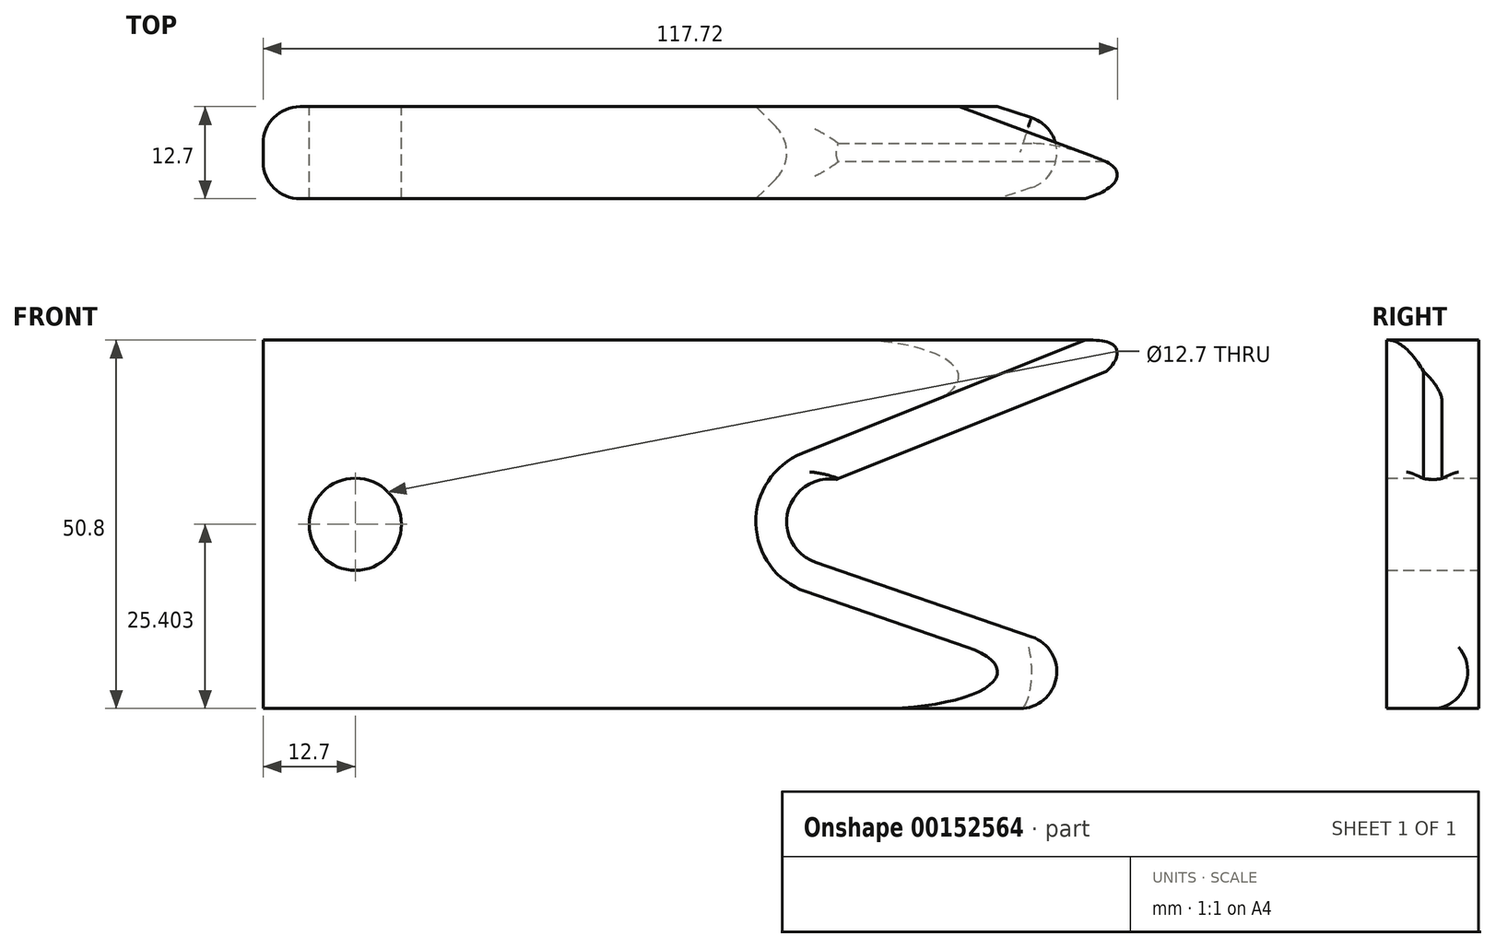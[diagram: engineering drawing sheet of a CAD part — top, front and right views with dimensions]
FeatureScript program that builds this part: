
annotation { "Feature Type Name" : "Feature", "Feature Type Description" : "" }
export const myFeature = defineFeature(function(context is Context, id is Id, definition is map)
    precondition{}
    {
        {
            var Q0;
            Q0=qCreatedBy(makeId("Front.planeOp"),FACE);
            var sketch = newSketch(context, id + "F0", { "sketchPlane" : qUnion([Q0])});
            skLineSegment(sketch, "E0.bottom", {"start": v(-69.8, 20.81) * mm, "end": v(57.2, 20.81) * mm});
            skLineSegment(sketch, "E0.top", {"start": v(-69.8, -29.99) * mm, "end": v(67.37, -29.99) * mm});
            skLineSegment(sketch, "E0.left", {"start": v(-69.8, 20.81) * mm, "end": v(-69.8, -29.99) * mm});
            skLineSegment(sketch, "E1", {"start": v(-6.3, -4.59) * mm, "end": v(57.2, 20.81) * mm});
            skPoint(sketch, "E1.startSnap0", {"position": v(-69.8, -4.59) * mm});
            skPoint(sketch, "E1.startSnap1", {"position": v(-6.3, 20.81) * mm});
            skLineSegment(sketch, "E2", {"start": v(-6.3, -4.59) * mm, "end": v(67.37, -29.99) * mm});
            skCircle(sketch, "E3", {"center": v(-57.1, -4.59) * mm, "radius": 6.35 * mm});
            skSolve(sketch);
        }
        {
            var Q0;
            Q0 = qSketchRegion(id + "F0", true);
            extrude(context, id + "F1", {"entities" : qUnion([Q0]), "depth" : 12.7 * mm});
        }
        {
            var Q0;
            Q0=makeQuery(id+"F1.opExtrude","SWEPT_EDGE",EDGE,{"disambiguationData":[OSD([sQuery(id+"F0.wireOp",EDGE,"E1"),sQuery(id+"F0.wireOp",EDGE,"E2")])]});
            fillet(context, id + "F2", {"entities" : qUnion([Q0]), "radius" : 5.08 * mm, "tangentPropagation" : true, "allowEdgeOverflow" : false});
        }
        {
            var Q0;
            Q0=makeQuery(id+"F2.opFillet","BLEND_FACE",FACE,{"disambiguationData":[OSD([sQuery(id+"F0.wireOp",EDGE,"E1"),sQuery(id+"F0.wireOp",EDGE,"E2")])]});
            chamfer(context, id + "F3", {"entities" : qUnion([Q0]), "width" : 5.08 * mm, "tangentPropagation" : true});
        }
        {
            var Q0;
            Q0=makeQuery(id+"F3.opChamfer","BLEND_EDGE",EDGE,{"blendedFrom":[makeQuery(id+"F1.opExtrude","CAP_EDGE",EDGE,{"disambiguationData":[OSD([sQuery(id+"F0.wireOp",EDGE,"E1")])],"isStart":true}),makeQuery(id+"F1.opExtrude","SWEPT_FACE",FACE,{"disambiguationData":[OSD([sQuery(id+"F0.wireOp",EDGE,"E0.bottom")])]})],"blendedInto":[makeQuery(id+"F1.opExtrude","SWEPT_FACE",FACE,{"disambiguationData":[OSD([sQuery(id+"F0.wireOp",EDGE,"E0.bottom")])]})]});
            fillet(context, id + "F4", {"entities" : qUnion([Q0]), "radius" : 5.08 * mm, "tangentPropagation" : true, "allowEdgeOverflow" : false});
        }
        {
            var Q0;
            Q0=makeQuery(id+"F3.opChamfer","BLEND_EDGE",EDGE,{"blendedFrom":[makeQuery(id+"F1.opExtrude","CAP_EDGE",EDGE,{"disambiguationData":[OSD([sQuery(id+"F0.wireOp",EDGE,"E2")])],"isStart":true}),makeQuery(id+"F1.opExtrude","SWEPT_FACE",FACE,{"disambiguationData":[OSD([sQuery(id+"F0.wireOp",EDGE,"E0.top")])]})],"blendedInto":[makeQuery(id+"F1.opExtrude","SWEPT_FACE",FACE,{"disambiguationData":[OSD([sQuery(id+"F0.wireOp",EDGE,"E0.top")])]})]});
            fillet(context, id + "F5", {"entities" : qUnion([Q0]), "radius" : 5.08 * mm, "tangentPropagation" : true, "allowEdgeOverflow" : false});
        }
        {
            var Q0;
            Q0=makeQuery(id+"F1.opExtrude","CAP_EDGE",EDGE,{"disambiguationData":[OSD([sQuery(id+"F0.wireOp",EDGE,"E0.left")])],"isStart":true});
            fillet(context, id + "F6", {"entities" : qUnion([Q0]), "radius" : 5.08 * mm, "tangentPropagation" : true, "allowEdgeOverflow" : false});
        }
        {
            var Q0;
            Q0=makeQuery(id+"F1.opExtrude","CAP_EDGE",EDGE,{"disambiguationData":[OSD([sQuery(id+"F0.wireOp",EDGE,"E0.left")])],"isStart":false});
            fillet(context, id + "F7", {"entities" : qUnion([Q0]), "radius" : 5.08 * mm, "tangentPropagation" : true, "allowEdgeOverflow" : false});
        }
        {
            var Q0;
            Q0=makeQuery(id+"F3.opChamfer","BLEND_EDGE",EDGE,{"blendedFrom":[makeQuery(id+"F1.opExtrude","CAP_EDGE",EDGE,{"disambiguationData":[OSD([sQuery(id+"F0.wireOp",EDGE,"E2")])],"isStart":false}),makeQuery(id+"F1.opExtrude","SWEPT_FACE",FACE,{"disambiguationData":[OSD([sQuery(id+"F0.wireOp",EDGE,"E0.top")])]})],"blendedInto":[makeQuery(id+"F1.opExtrude","SWEPT_FACE",FACE,{"disambiguationData":[OSD([sQuery(id+"F0.wireOp",EDGE,"E0.top")])]})]});
            fillet(context, id + "F8", {"entities" : qUnion([Q0]), "radius" : 5.08 * mm, "tangentPropagation" : true, "allowEdgeOverflow" : false});
        }
    });
